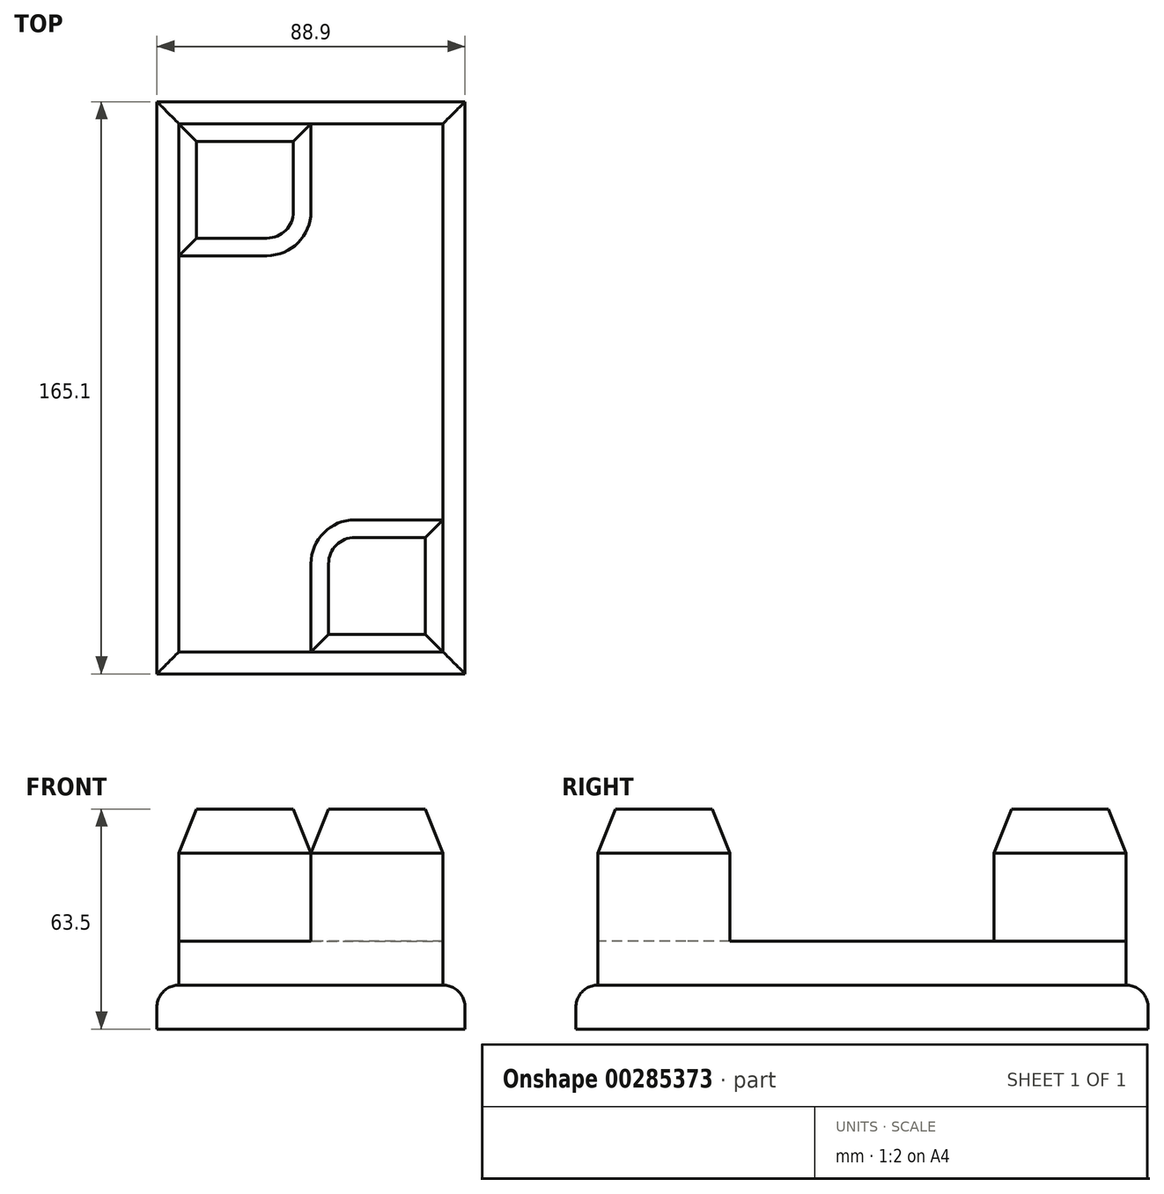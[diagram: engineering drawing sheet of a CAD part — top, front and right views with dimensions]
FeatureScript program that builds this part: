
annotation { "Feature Type Name" : "Feature", "Feature Type Description" : "" }
export const myFeature = defineFeature(function(context is Context, id is Id, definition is map)
    precondition{}
    {
        {
            var Q0;
            Q0=qCreatedBy(makeId("Top.planeOp"),FACE);
            var sketch = newSketch(context, id + "F0", { "sketchPlane" : qUnion([Q0])});
            skLineSegment(sketch, "E0", {"start": v(-38.1, 0) * mm, "end": v(-38.1, 75.9) * mm});
            skLineSegment(sketch, "E1.bottom", {"start": v(-38.1, 75.9) * mm, "end": v(38.1, 75.9) * mm});
            skLineSegment(sketch, "E1.top", {"start": v(-38.1, -76.5) * mm, "end": v(38.1, -76.5) * mm});
            skLineSegment(sketch, "E1.left", {"start": v(-38.1, 0) * mm, "end": v(-38.1, -76.5) * mm});
            skLineSegment(sketch, "E1.right", {"start": v(38.1, 75.9) * mm, "end": v(38.1, -76.5) * mm});
            skPoint(sketch, "E2.center.orphan", {"position": v(0, 0) * mm});
            skPoint(sketch, "E3.center.orphan", {"position": v(38.1, 0) * mm});
            skLineSegment(sketch, "E4.0", {"start": v(-38.1, 37.8) * mm, "end": v(-12.7, 37.8) * mm});
            skLineSegment(sketch, "E5", {"start": v(0, 50.5) * mm, "end": v(0, 75.9) * mm});
            skPoint(sketch, "E6.orphan", {"position": v(38.1, 37.8) * mm});
            skPoint(sketch, "E7.visualSharp", {"position": v(0, 37.8) * mm});
            skArc(sketch, "E7.filletArc", {"start": v(-12.7, 37.8) * mm, "mid": v(-3.72, 41.52) * mm, "end": v(0, 50.5) * mm});
            skLineSegment(sketch, "E8", {"start": v(0, -76.5) * mm, "end": v(0, -51.1) * mm});
            skLineSegment(sketch, "E9", {"start": v(12.7, -38.4) * mm, "end": v(38.1, -38.4) * mm});
            skPoint(sketch, "E10.visualSharp", {"position": v(0, -38.4) * mm});
            skArc(sketch, "E10.filletArc", {"start": v(12.7, -38.4) * mm, "mid": v(3.72, -42.12) * mm, "end": v(0, -51.1) * mm});
            skLineSegment(sketch, "E11.0", {"start": v(-38.1, 82.25) * mm, "end": v(38.06, 82.25) * mm});
            skLineSegment(sketch, "E12", {"start": v(-44.45, 76.2) * mm, "end": v(-44.45, 82.25) * mm});
            skLineSegment(sketch, "E13", {"start": v(-44.45, 82.25) * mm, "end": v(-38.1, 82.25) * mm});
            skLineSegment(sketch, "E14.1", {"start": v(-38.1, -82.85) * mm, "end": v(44.45, -82.85) * mm});
            skLineSegment(sketch, "E15.bottom", {"start": v(38.06, 82.25) * mm, "end": v(44.45, 82.25) * mm});
            skLineSegment(sketch, "E15.top", {"start": v(-44.45, -82.85) * mm, "end": v(-38.1, -82.85) * mm});
            skLineSegment(sketch, "E15.left", {"start": v(-44.45, 76.2) * mm, "end": v(-44.45, -82.85) * mm});
            skLineSegment(sketch, "E15.right", {"start": v(44.45, 82.25) * mm, "end": v(44.45, -82.85) * mm});
            skSolve(sketch);
        }
        {
            var Q0;
            Q0 = qSketchRegion(id + "F0", true);
            var Q1;
            {var subQ1=sQuery(id+"F0.wireOp",EDGE,"E4.0");Q1=makeQuery(id+"F0.imprint","IMPRINT",FACE,{"disambiguationData":[TD([[makeQuery(id+"F0.imprint","IMPRINT",EDGE,{"derivedFrom":subQ1}),1.0]])]});}
            var Q2;
            {var subQ7=sQuery(id+"F0.wireOp",EDGE,"E1.left");Q2=makeQuery(id+"F0.imprint","IMPRINT",FACE,{"disambiguationData":[TD([[makeQuery(id+"F0.imprint","IMPRINT",EDGE,{"derivedFrom":subQ7}),1.0]])]});}
            var Q3;
            {var subQ0=sQuery(id+"F0.wireOp",EDGE,"E8");Q3=makeQuery(id+"F0.imprint","IMPRINT",FACE,{"disambiguationData":[TD([[makeQuery(id+"F0.imprint","IMPRINT",EDGE,{"derivedFrom":subQ0}),-1.0]])]});}
            extrude(context, id + "F1", {"entities" : qUnion([Q0, Q1, Q2, Q3]), "depth" : 12.7 * mm});
        }
        {
            var Q0;
            {var subQ0=sQuery(id+"F0.wireOp",EDGE,"E8");Q0=makeQuery(id+"F0.imprint","IMPRINT",FACE,{"disambiguationData":[TD([[makeQuery(id+"F0.imprint","IMPRINT",EDGE,{"derivedFrom":subQ0}),-1.0]])]});}
            var Q1;
            {var subQ7=sQuery(id+"F0.wireOp",EDGE,"E1.left");Q1=makeQuery(id+"F0.imprint","IMPRINT",FACE,{"disambiguationData":[TD([[makeQuery(id+"F0.imprint","IMPRINT",EDGE,{"derivedFrom":subQ7}),1.0]])]});}
            var Q2;
            {var subQ1=sQuery(id+"F0.wireOp",EDGE,"E4.0");Q2=makeQuery(id+"F0.imprint","IMPRINT",FACE,{"disambiguationData":[TD([[makeQuery(id+"F0.imprint","IMPRINT",EDGE,{"derivedFrom":subQ1}),1.0]])]});}
            extrude(context, id + "F2", {"entities" : qUnion([Q0, Q1, Q2]), "operationType" : NewBodyOperationType.ADD, "depth" : 25.4 * mm});
        }
        {
            var Q0;
            {var subQ0=sQuery(id+"F0.wireOp",EDGE,"E8");Q0=makeQuery(id+"F0.imprint","IMPRINT",FACE,{"disambiguationData":[TD([[makeQuery(id+"F0.imprint","IMPRINT",EDGE,{"derivedFrom":subQ0}),-1.0]])]});}
            var Q1;
            {var subQ1=sQuery(id+"F0.wireOp",EDGE,"E4.0");Q1=makeQuery(id+"F0.imprint","IMPRINT",FACE,{"disambiguationData":[TD([[makeQuery(id+"F0.imprint","IMPRINT",EDGE,{"derivedFrom":subQ1}),1.0]])]});}
            extrude(context, id + "F3", {"entities" : qUnion([Q0, Q1]), "operationType" : NewBodyOperationType.ADD, "depth" : 63.5 * mm});
        }
        {
            var Q0;
            Q0=makeQuery(id+"F1.opExtrude","CAP_EDGE",EDGE,{"disambiguationData":[OSD([sQuery(id+"F0.wireOp",EDGE,"E12"),sQuery(id+"F0.wireOp",EDGE,"E15.left")])],"isStart":false});
            var Q1;
            Q1=makeQuery(id+"F1.opExtrude","CAP_EDGE",EDGE,{"disambiguationData":[OSD([sQuery(id+"F0.wireOp",EDGE,"E14.1"),sQuery(id+"F0.wireOp",EDGE,"E15.top")])],"isStart":false});
            var Q2;
            Q2=makeQuery(id+"F1.opExtrude","CAP_EDGE",EDGE,{"disambiguationData":[OSD([sQuery(id+"F0.wireOp",EDGE,"E15.right")])],"isStart":false});
            var Q3;
            Q3=makeQuery(id+"F1.opExtrude","CAP_EDGE",EDGE,{"disambiguationData":[OSD([sQuery(id+"F0.wireOp",EDGE,"E11.0"),sQuery(id+"F0.wireOp",EDGE,"E13"),sQuery(id+"F0.wireOp",EDGE,"E15.bottom")])],"isStart":false});
            fillet(context, id + "F4", {"entities" : qUnion([Q0, Q1, Q2, Q3]), "radius" : 6.35 * mm, "tangentPropagation" : true, "allowEdgeOverflow" : false});
        }
        {
            var Q0;
            Q0=makeQuery(id+"F3.opExtrude","CAP_FACE",FACE,{"disambiguationData":[OSD([sQuery(id+"F0.wireOp",EDGE,"E1.top"),sQuery(id+"F0.wireOp",EDGE,"E1.right"),sQuery(id+"F0.wireOp",EDGE,"E8"),sQuery(id+"F0.wireOp",EDGE,"E9"),sQuery(id+"F0.wireOp",EDGE,"E10.filletArc")])],"isStart":false});
            chamfer(context, id + "F5", {"entities" : qUnion([Q0]), "chamferType" : ChamferType.TWO_OFFSETS, "width1" : 5.08 * mm, "oppositeDirection" : false, "width2" : 12.7 * mm, "tangentPropagation" : true});
        }
        {
            var Q0;
            Q0=makeQuery(id+"F3.opExtrude","CAP_FACE",FACE,{"disambiguationData":[OSD([sQuery(id+"F0.wireOp",EDGE,"E0"),sQuery(id+"F0.wireOp",EDGE,"E1.bottom"),sQuery(id+"F0.wireOp",EDGE,"E4.0"),sQuery(id+"F0.wireOp",EDGE,"E5"),sQuery(id+"F0.wireOp",EDGE,"E7.filletArc")])],"isStart":false});
            chamfer(context, id + "F6", {"entities" : qUnion([Q0]), "chamferType" : ChamferType.TWO_OFFSETS, "width1" : 12.7 * mm, "oppositeDirection" : false, "width2" : 5.08 * mm, "tangentPropagation" : true});
        }
    });
